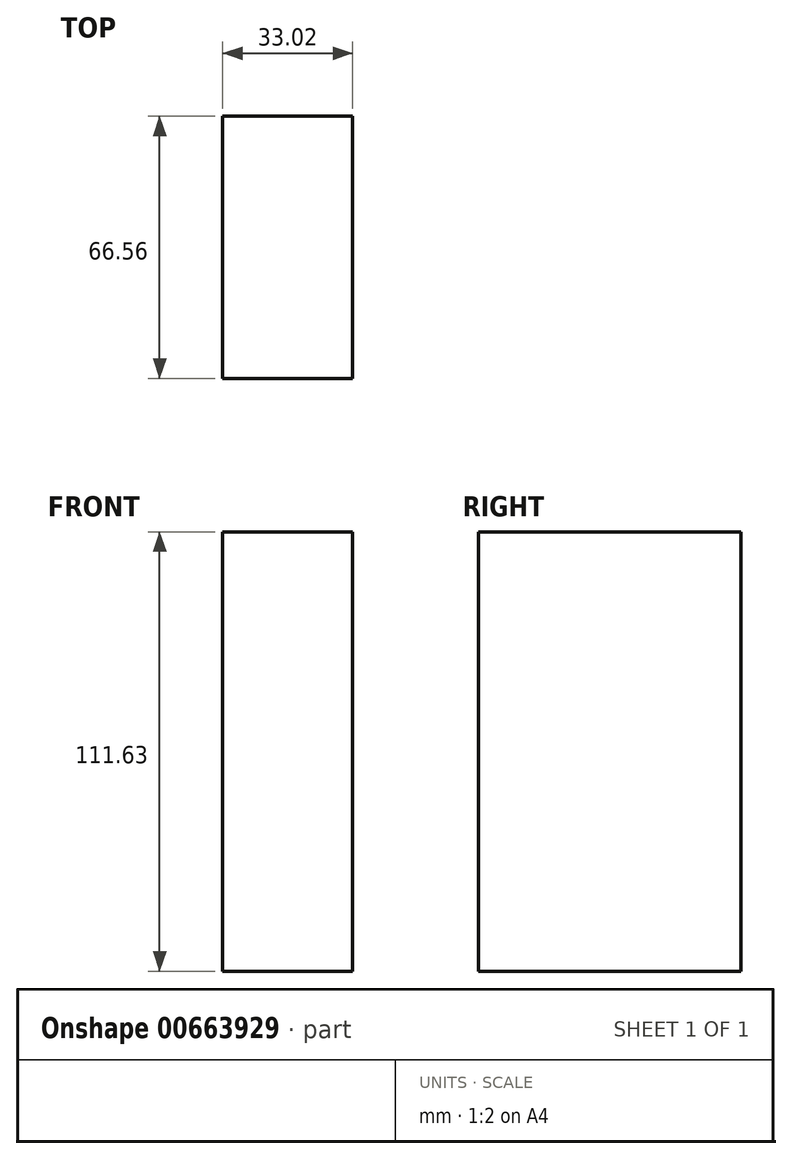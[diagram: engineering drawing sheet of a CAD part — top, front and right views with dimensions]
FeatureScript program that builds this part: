
annotation { "Feature Type Name" : "Feature", "Feature Type Description" : "" }
export const myFeature = defineFeature(function(context is Context, id is Id, definition is map)
    precondition{}
    {
        {
            var Q0;
            Q0=qCreatedBy(makeId("Right.planeOp"),FACE);
            var sketch = newSketch(context, id + "F0", { "sketchPlane" : qUnion([Q0])});
            skLineSegment(sketch, "E0.bottom", {"start": v(-98.99, 65.69) * mm, "end": v(-32.43, 65.69) * mm});
            skLineSegment(sketch, "E0.top", {"start": v(-98.99, -45.94) * mm, "end": v(-32.43, -45.94) * mm});
            skLineSegment(sketch, "E0.left", {"start": v(-98.99, 65.69) * mm, "end": v(-98.99, -45.94) * mm});
            skLineSegment(sketch, "E0.right", {"start": v(-32.43, 65.69) * mm, "end": v(-32.43, -45.94) * mm});
            skSolve(sketch);
        }
        {
            var Q0;
            Q0=makeQuery(id+"F0.imprint","IMPRINT",FACE,{"disambiguationData":[TD([[makeQuery(id+"F0.imprint","IMPRINT",EDGE,{"derivedFrom":sQuery(id+"F0.wireOp",EDGE,"E0.bottom")}),-1.0]])]});
            extrude(context, id + "F1", {"entities" : qUnion([Q0]), "depth" : 33.02 * mm, "offsetDistance" : 25.4 * mm});
        }
    });
